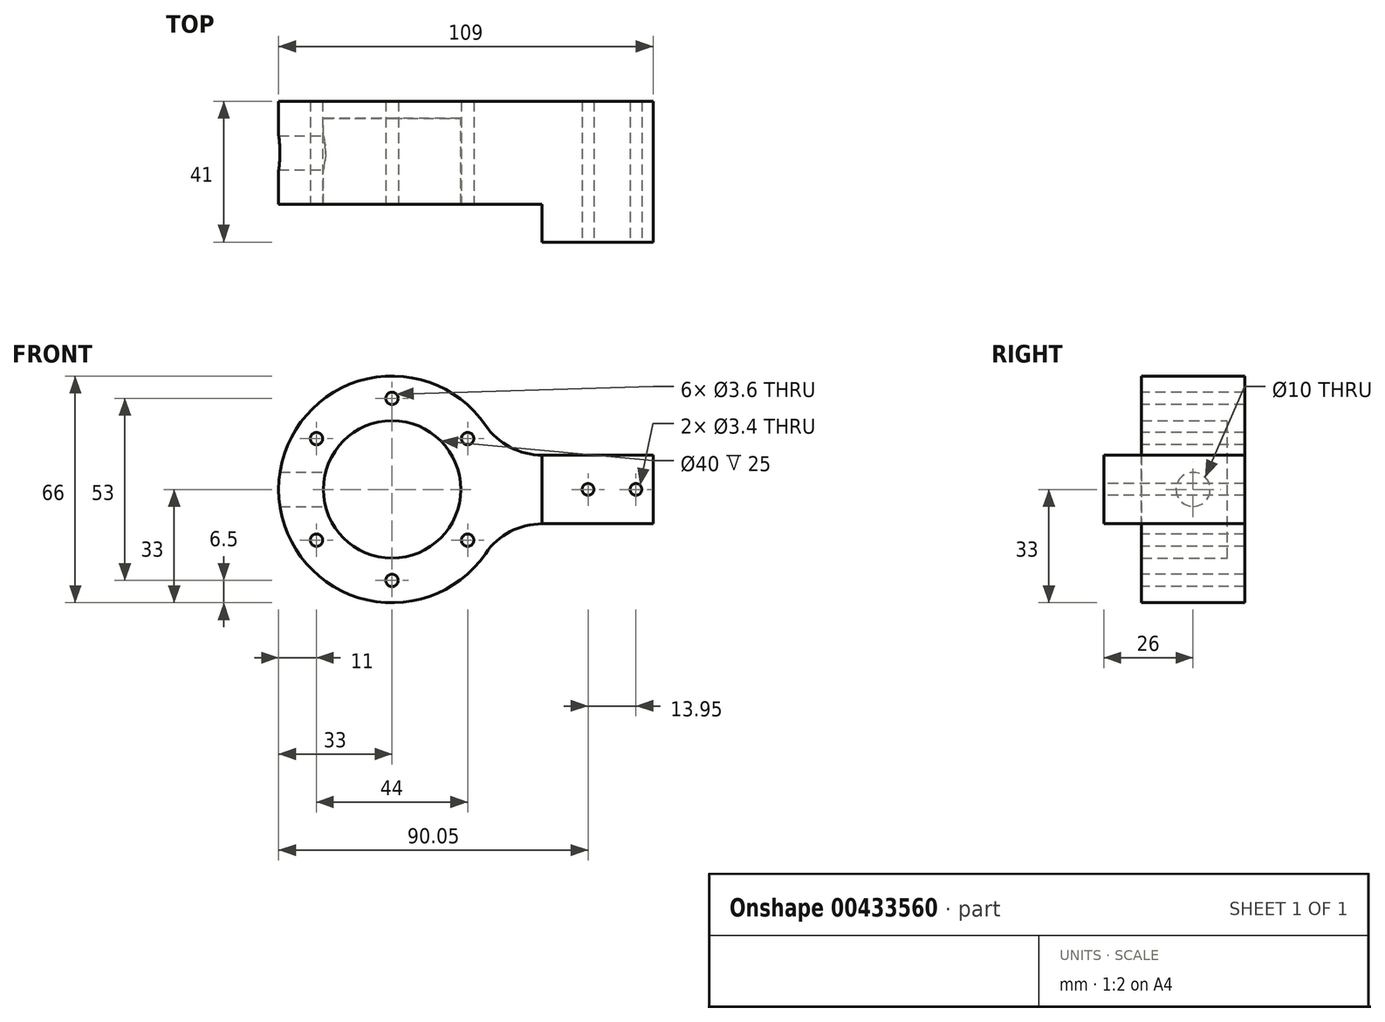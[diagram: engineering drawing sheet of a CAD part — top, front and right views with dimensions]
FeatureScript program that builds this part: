
annotation { "Feature Type Name" : "Feature", "Feature Type Description" : "" }
export const myFeature = defineFeature(function(context is Context, id is Id, definition is map)
    precondition{}
    {
        {
            var Q0;
            Q0=qCreatedBy(makeId("Front.planeOp"),FACE);
            var sketch = newSketch(context, id + "F0", { "sketchPlane" : qUnion([Q0])});
            skCircle(sketch, "E0", {"center": v(0, 0) * mm, "radius": 33 * mm});
            skSolve(sketch);
        }
        {
            var Q0;
            Q0 = qSketchRegion(id + "F0", true);
            extrude(context, id + "F1", {"entities" : qUnion([Q0]), "depth" : 5 * mm});
        }
        {
            var Q0;
            Q0=makeQuery(id+"F1.opExtrude","CAP_FACE",FACE,{"disambiguationData":[OSD([sQuery(id+"F0.wireOp",EDGE,"E0")])],"isStart":false});
            var sketch = newSketch(context, id + "F2", { "sketchPlane" : qUnion([Q0])});
            skCircle(sketch, "E1", {"center": v(0, 0) * mm, "radius": 20 * mm});
            skSolve(sketch);
        }
        {
            var Q0;
            Q0=makeQuery(id+"F2.imprint","IMPRINT",FACE,{"disambiguationData":[TD([[makeQuery(id+"F2.imprint","IMPRINT",EDGE,{"derivedFrom":sQuery(id+"F2.wireOp",EDGE,"E1")}),-1.0]])]});
            extrude(context, id + "F3", {"entities" : qUnion([Q0]), "operationType" : NewBodyOperationType.ADD, "depth" : 25 * mm});
        }
        {
            var Q0;
            Q0=makeQuery(id+"F3.opExtrude","CAP_FACE",FACE,{"disambiguationData":[OSD([sQuery(id+"F0.wireOp",EDGE,"E0"),sQuery(id+"F2.wireOp",EDGE,"E1")])],"isStart":false});
            var sketch = newSketch(context, id + "F4", { "sketchPlane" : qUnion([Q0])});
            skCircle(sketch, "E2", {"center": v(0, 26.5) * mm, "radius": 1.8 * mm});
            skCircle(sketch, "E3", {"center": v(22, 14.77) * mm, "radius": 1.8 * mm});
            skCircle(sketch, "E4", {"center": v(-22, 14.77) * mm, "radius": 1.8 * mm});
            skCircle(sketch, "E5", {"center": v(0, -26.5) * mm, "radius": 1.8 * mm});
            skCircle(sketch, "E6", {"center": v(-22, -14.77) * mm, "radius": 1.8 * mm});
            skCircle(sketch, "E7", {"center": v(22, -14.77) * mm, "radius": 1.8 * mm});
            skSolve(sketch);
        }
        {
            var Q0;
            Q0 = qSketchRegion(id + "F4", true);
            extrude(context, id + "F5", {"entities" : qUnion([Q0]), "operationType" : NewBodyOperationType.REMOVE, "endBound" : BoundingType.THROUGH_ALL, "oppositeDirection" : true, "depth" : 20 * mm});
        }
        {
            var Q0;
            Q0=qCreatedBy(makeId("Right.planeOp"),FACE);
            cPlane(context, id + "F6", {"entities" : qUnion([Q0]), "cplaneType" : CPlaneType.OFFSET, "offset" : 29 * mm, "width" : 150 * mm, "height" : 150 * mm});
        }
        {
            var Q0;
            Q0=qCreatedBy(id+"F6.planeOp",FACE);
            var sketch = newSketch(context, id + "F7", { "sketchPlane" : qUnion([Q0])});
            skLineSegment(sketch, "E8", {"start": v(0, 10) * mm, "end": v(0, -10) * mm});
            skLineSegment(sketch, "E9", {"start": v(0, -10) * mm, "end": v(-20, -10) * mm});
            skLineSegment(sketch, "E10", {"start": v(-20, -10) * mm, "end": v(-20, 10) * mm});
            skLineSegment(sketch, "E11", {"start": v(-20, 10) * mm, "end": v(0, 10) * mm});
            skSolve(sketch);
        }
        {
            var Q0;
            Q0 = qSketchRegion(id + "F7", true);
            var Q1;
            Q1 = qSketchRegion(id + "F9", true);
            extrude(context, id + "F8", {"entities" : qUnion([Q0, Q1]), "operationType" : NewBodyOperationType.ADD, "depth" : 52 * mm});
        }
        {
            var Q0;
            Q0=makeQuery(id+"F8.opExtrude","SWEPT_FACE",FACE,{"disambiguationData":[OSD([sQuery(id+"F7.wireOp",EDGE,"E10")])]});
            var sketch = newSketch(context, id + "F9", { "sketchPlane" : qUnion([Q0])});
            skPoint(sketch, "E12.oppositeSnap0", {"position": v(56.22, -10) * mm});
            skLineSegment(sketch, "E12.bottom", {"start": v(81, 10) * mm, "end": v(29, 10) * mm});
            skLineSegment(sketch, "E12.top", {"start": v(81, -10) * mm, "end": v(29, -10) * mm});
            skLineSegment(sketch, "E12.left", {"start": v(81, 10) * mm, "end": v(81, -10) * mm});
            skLineSegment(sketch, "E12.right", {"start": v(29, 10) * mm, "end": v(29, -10) * mm});
            skSolve(sketch);
        }
        {
            var Q0;
            Q0=qCreatedBy(makeId("Right.planeOp"),FACE);
            cPlane(context, id + "F10", {"entities" : qUnion([Q0]), "cplaneType" : CPlaneType.OFFSET, "offset" : 21 * mm, "oppositeDirection" : true, "width" : 150 * mm, "height" : 150 * mm});
        }
        {
            var Q0;
            Q0=qCreatedBy(id+"F10.planeOp",FACE);
            var sketch = newSketch(context, id + "F11", { "sketchPlane" : qUnion([Q0])});
            skCircle(sketch, "E13", {"center": v(-15, 0) * mm, "radius": 5 * mm});
            skSolve(sketch);
        }
        {
            var Q0;
            Q0 = qSketchRegion(id + "F9", true);
            extrude(context, id + "F12", {"entities" : qUnion([Q0]), "operationType" : NewBodyOperationType.ADD, "depth" : 10 * mm});
        }
        {
            var Q0;
            Q0 = qSketchRegion(id + "FxaWf7fYDkgSvOb_1", true);
            var Q1;
            Q1 = qSketchRegion(id + "F11", true);
            extrude(context, id + "F13", {"entities" : qUnion([Q0, Q1]), "operationType" : NewBodyOperationType.REMOVE, "endBound" : BoundingType.THROUGH_ALL, "oppositeDirection" : true, "depth" : 25 * mm, "hasSecondDirection" : true, "secondDirectionOppositeDirection" : false, "secondDirectionDepth" : 10 * mm});
        }
        {
            var Q0;
            {var subQ0=sQuery(id+"F0.wireOp",EDGE,"E0");Q0=makeQuery(id+"F12.boolean.opBoolean","INTERSECT",EDGE,{"derivedFrom":[makeQuery(id+"F3.boolean.opBoolean","MERGE",FACE,{"derivedFrom":[makeQuery(id+"F1.opExtrude","SWEPT_FACE",FACE,{"disambiguationData":[OSD([subQ0])]}),makeQuery(id+"F3.opExtrude","SWEPT_FACE",FACE,{"disambiguationData":[OSD([subQ0])]})]}),makeQuery(id+"F12.opExtrude","SWEPT_FACE",FACE,{"disambiguationData":[OSD([sQuery(id+"F9.wireOp",EDGE,"E12.top")])]})]});}
            var Q1;
            {var subQ0=sQuery(id+"F0.wireOp",EDGE,"E0");Q1=makeQuery(id+"F12.boolean.opBoolean","INTERSECT",EDGE,{"derivedFrom":[makeQuery(id+"F3.boolean.opBoolean","MERGE",FACE,{"derivedFrom":[makeQuery(id+"F1.opExtrude","SWEPT_FACE",FACE,{"disambiguationData":[OSD([subQ0])]}),makeQuery(id+"F3.opExtrude","SWEPT_FACE",FACE,{"disambiguationData":[OSD([subQ0])]})]}),makeQuery(id+"F12.opExtrude","SWEPT_FACE",FACE,{"disambiguationData":[OSD([sQuery(id+"F9.wireOp",EDGE,"E12.bottom")])]})]});}
            fillet(context, id + "F14", {"entities" : qUnion([Q0, Q1]), "radius" : 20 * mm, "tangentPropagation" : true, "allowEdgeOverflow" : false});
        }
        {
            var Q0;
            Q0=makeQuery(id+"F12.boolean.opBoolean","MERGE",FACE,{"derivedFrom":[makeQuery(id+"F3.opExtrude","CAP_FACE",FACE,{"disambiguationData":[OSD([sQuery(id+"F0.wireOp",EDGE,"E0"),sQuery(id+"F2.wireOp",EDGE,"E1")])],"isStart":false}),makeQuery(id+"F12.opExtrude","CAP_FACE",FACE,{"disambiguationData":[OSD([sQuery(id+"F9.wireOp",EDGE,"E12.bottom"),sQuery(id+"F9.wireOp",EDGE,"E12.top"),sQuery(id+"F9.wireOp",EDGE,"E12.left"),sQuery(id+"F9.wireOp",EDGE,"E12.right")])],"isStart":false})]});
            var sketch = newSketch(context, id + "F15", { "sketchPlane" : qUnion([Q0])});
            skLineSegment(sketch, "E14.bottom", {"start": v(81, 10) * mm, "end": v(61, 10) * mm});
            skLineSegment(sketch, "E14.top", {"start": v(81, -10) * mm, "end": v(61, -10) * mm});
            skLineSegment(sketch, "E14.left", {"start": v(81, 10) * mm, "end": v(81, -10) * mm});
            skLineSegment(sketch, "E14.right", {"start": v(61, 10) * mm, "end": v(61, -10) * mm});
            skSolve(sketch);
        }
        {
            var Q0;
            Q0 = qSketchRegion(id + "F15", true);
            extrude(context, id + "F16", {"entities" : qUnion([Q0]), "operationType" : NewBodyOperationType.ADD, "depth" : 11 * mm});
        }
        {
            var Q0;
            Q0=makeQuery(id+"F16.opExtrude","CAP_FACE",FACE,{"disambiguationData":[OSD([sQuery(id+"F15.wireOp",EDGE,"E14.bottom"),sQuery(id+"F15.wireOp",EDGE,"E14.top"),sQuery(id+"F15.wireOp",EDGE,"E14.left"),sQuery(id+"F15.wireOp",EDGE,"E14.right")])],"isStart":false});
            var sketch = newSketch(context, id + "F17", { "sketchPlane" : qUnion([Q0])});
            skCircle(sketch, "E15", {"center": v(71, 0) * mm, "radius": 1.7 * mm});
            skSolve(sketch);
        }
        {
            var Q0;
            Q0 = qSketchRegion(id + "F17", true);
            extrude(context, id + "F18", {"entities" : qUnion([Q0]), "operationType" : NewBodyOperationType.REMOVE, "endBound" : BoundingType.THROUGH_ALL, "oppositeDirection" : true, "depth" : 25 * mm});
        }
        {
            var Q0;
            Q0=makeQuery(id+"F12.boolean.opBoolean","MERGE",FACE,{"derivedFrom":[makeQuery(id+"F3.opExtrude","CAP_FACE",FACE,{"disambiguationData":[OSD([sQuery(id+"F0.wireOp",EDGE,"E0"),sQuery(id+"F2.wireOp",EDGE,"E1")])],"isStart":false}),makeQuery(id+"F12.opExtrude","CAP_FACE",FACE,{"disambiguationData":[OSD([sQuery(id+"F9.wireOp",EDGE,"E12.bottom"),sQuery(id+"F9.wireOp",EDGE,"E12.top"),sQuery(id+"F9.wireOp",EDGE,"E12.left"),sQuery(id+"F9.wireOp",EDGE,"E12.right")])],"isStart":false})]});
            var sketch = newSketch(context, id + "F19", { "sketchPlane" : qUnion([Q0])});
            skLineSegment(sketch, "E16.bottom", {"start": v(61, 10) * mm, "end": v(43.7, 10) * mm});
            skLineSegment(sketch, "E16.top", {"start": v(61, -10) * mm, "end": v(43.7, -10) * mm});
            skLineSegment(sketch, "E16.left", {"start": v(61, 10) * mm, "end": v(61, -10) * mm});
            skLineSegment(sketch, "E16.right", {"start": v(43.7, 10) * mm, "end": v(43.7, -10) * mm});
            skSolve(sketch);
        }
        {
            var Q0;
            Q0 = qSketchRegion(id + "F19", true);
            extrude(context, id + "F20", {"entities" : qUnion([Q0]), "operationType" : NewBodyOperationType.ADD, "depth" : 11 * mm});
        }
        {
            var Q0;
            Q0=makeQuery(id+"F20.boolean.opBoolean","MERGE",FACE,{"derivedFrom":[makeQuery(id+"F16.opExtrude","CAP_FACE",FACE,{"disambiguationData":[OSD([sQuery(id+"F15.wireOp",EDGE,"E14.bottom"),sQuery(id+"F15.wireOp",EDGE,"E14.top"),sQuery(id+"F15.wireOp",EDGE,"E14.left"),sQuery(id+"F15.wireOp",EDGE,"E14.right")])],"isStart":false}),makeQuery(id+"F20.opExtrude","CAP_FACE",FACE,{"disambiguationData":[OSD([sQuery(id+"F19.wireOp",EDGE,"E16.bottom"),sQuery(id+"F19.wireOp",EDGE,"E16.top"),sQuery(id+"F19.wireOp",EDGE,"E16.left"),sQuery(id+"F19.wireOp",EDGE,"E16.right")])],"isStart":false})]});
            var sketch = newSketch(context, id + "F21", { "sketchPlane" : qUnion([Q0])});
            skCircle(sketch, "E17", {"center": v(57.05, 0) * mm, "radius": 1.7 * mm});
            skSolve(sketch);
        }
        {
            var Q0;
            Q0 = qSketchRegion(id + "F21", true);
            extrude(context, id + "F22", {"entities" : qUnion([Q0]), "operationType" : NewBodyOperationType.REMOVE, "endBound" : BoundingType.THROUGH_ALL, "oppositeDirection" : true, "depth" : 25 * mm, "offsetDistance" : 25 * mm});
        }
        {
            var Q0;
            Q0=makeQuery(id+"F20.boolean.opBoolean","MERGE",FACE,{"derivedFrom":[makeQuery(id+"F16.opExtrude","CAP_FACE",FACE,{"disambiguationData":[OSD([sQuery(id+"F15.wireOp",EDGE,"E14.bottom"),sQuery(id+"F15.wireOp",EDGE,"E14.top"),sQuery(id+"F15.wireOp",EDGE,"E14.left"),sQuery(id+"F15.wireOp",EDGE,"E14.right")])],"isStart":false}),makeQuery(id+"F20.opExtrude","CAP_FACE",FACE,{"disambiguationData":[OSD([sQuery(id+"F19.wireOp",EDGE,"E16.bottom"),sQuery(id+"F19.wireOp",EDGE,"E16.top"),sQuery(id+"F19.wireOp",EDGE,"E16.left"),sQuery(id+"F19.wireOp",EDGE,"E16.right")])],"isStart":false})]});
            var sketch = newSketch(context, id + "F23", { "sketchPlane" : qUnion([Q0])});
            skLineSegment(sketch, "E18.bottom", {"start": v(81, -10) * mm, "end": v(76, -10) * mm});
            skLineSegment(sketch, "E18.top", {"start": v(81, 10) * mm, "end": v(76, 10) * mm});
            skLineSegment(sketch, "E18.left", {"start": v(81, -10) * mm, "end": v(81, 10) * mm});
            skLineSegment(sketch, "E18.right", {"start": v(76, -10) * mm, "end": v(76, 10) * mm});
            skSolve(sketch);
        }
        {
            var Q0;
            Q0 = qSketchRegion(id + "F23", true);
            extrude(context, id + "F24", {"entities" : qUnion([Q0]), "operationType" : NewBodyOperationType.REMOVE, "endBound" : BoundingType.THROUGH_ALL, "oppositeDirection" : true, "depth" : 25 * mm});
        }
    });
